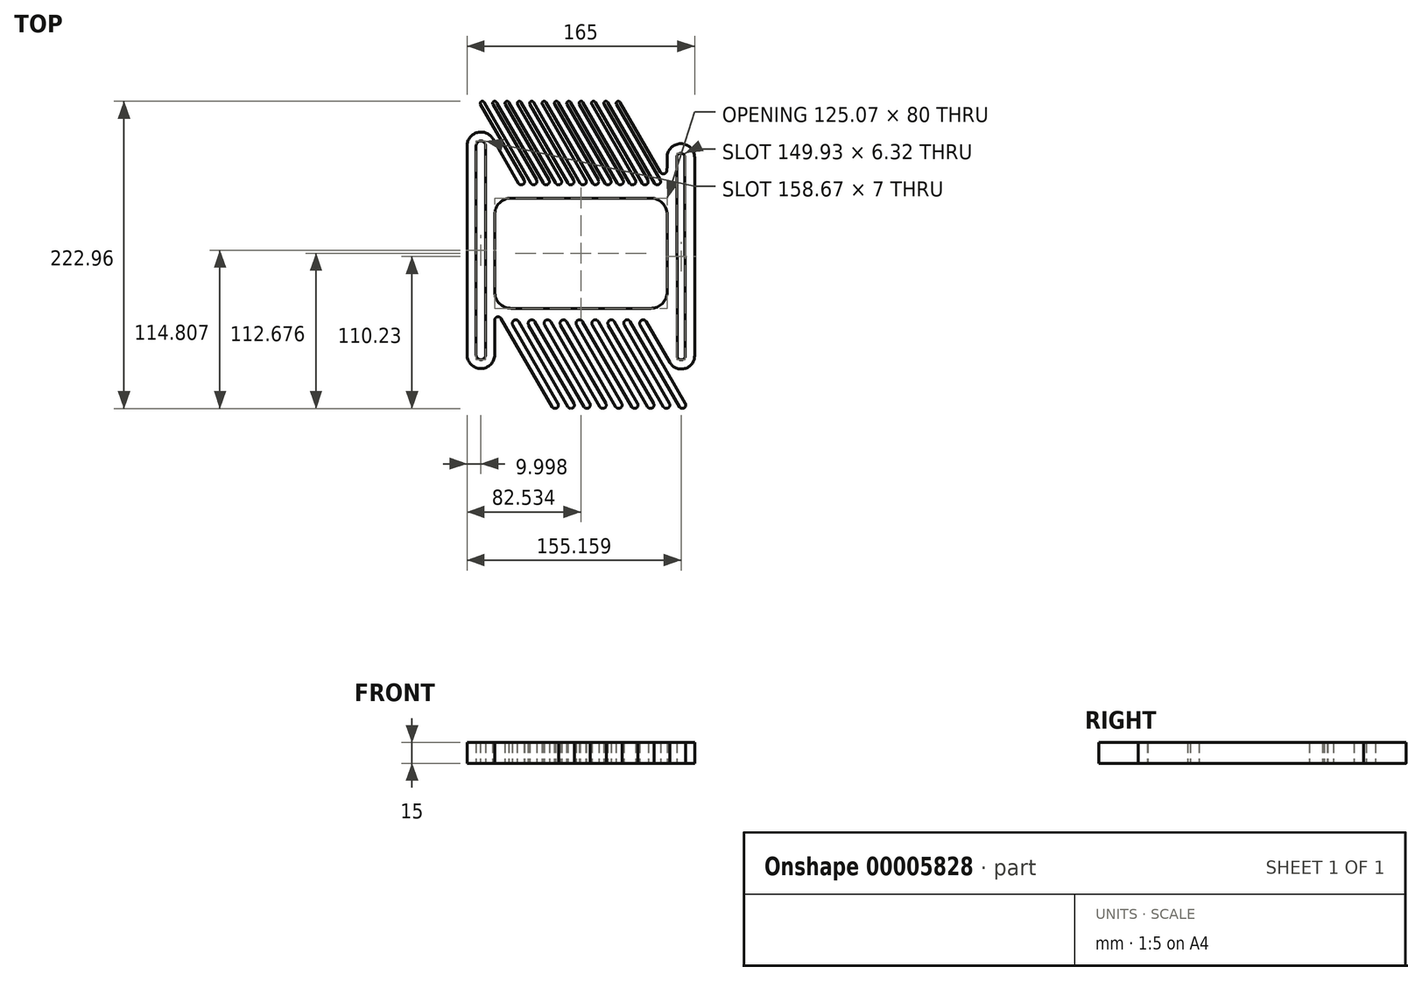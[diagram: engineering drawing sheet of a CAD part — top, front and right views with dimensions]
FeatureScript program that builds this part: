
annotation { "Feature Type Name" : "Feature", "Feature Type Description" : "" }
export const myFeature = defineFeature(function(context is Context, id is Id, definition is map)
    precondition{}
    {
        {
            var Q0;
            Q0=qCreatedBy(makeId("Top.planeOp"),FACE);
            var sketch = newSketch(context, id + "F0", { "sketchPlane" : qUnion([Q0])});
            skLineSegment(sketch, "E0.left", {"start": v(-82.57, 75.85) * mm, "end": v(-82.57, -75.82) * mm});
            skLineSegment(sketch, "E0.right", {"start": v(-62.57, 25.89) * mm, "end": v(-62.57, -30.11) * mm});
            skArc(sketch, "E1", {"start": v(-63.91, 80.85) * mm, "mid": v(-75.16, 85.51) * mm, "end": v(-82.57, 75.85) * mm});
            skArc(sketch, "E2", {"start": v(-82.57, -75.82) * mm, "mid": v(-72.57, -85.82) * mm, "end": v(-62.57, -75.82) * mm});
            skLineSegment(sketch, "E3.left", {"start": v(62.43, 67.4) * mm, "end": v(62.43, 59.57) * mm});
            skLineSegment(sketch, "E3.right", {"start": v(82.43, 67.4) * mm, "end": v(82.43, -76.53) * mm});
            skArc(sketch, "E4", {"start": v(82.43, 67.4) * mm, "mid": v(72.43, 77.4) * mm, "end": v(62.43, 67.4) * mm});
            skArc(sketch, "E5", {"start": v(64.37, -81.36) * mm, "mid": v(75.26, -85.87) * mm, "end": v(82.43, -76.53) * mm});
            skLineSegment(sketch, "E6.top", {"start": v(50.5, 37.89) * mm, "end": v(-50.57, 37.89) * mm});
            skLineSegment(sketch, "E7.bottom", {"start": v(-50.57, -42.11) * mm, "end": v(50.5, -42.11) * mm});
            skLineSegment(sketch, "E8", {"start": v(72.43, 67.4) * mm, "end": v(72.75, -76.53) * mm, "construction": true});
            skLineSegment(sketch, "E9", {"start": v(-72.57, -75.82) * mm, "end": v(-72.57, 75.85) * mm, "construction": true});
            skArc(sketch, "E10.0.startCap", {"start": v(-69.07, -75.82) * mm, "mid": v(-72.57, -79.32) * mm, "end": v(-76.07, -75.82) * mm});
            skArc(sketch, "E10.0.endCap", {"start": v(-76.07, 75.85) * mm, "mid": v(-72.57, 79.35) * mm, "end": v(-69.07, 75.85) * mm});
            skLineSegment(sketch, "E10.0.left", {"start": v(-76.07, -75.82) * mm, "end": v(-76.07, 75.85) * mm});
            skLineSegment(sketch, "E10.0.right", {"start": v(-69.07, -75.82) * mm, "end": v(-69.07, 75.85) * mm});
            skArc(sketch, "E11.0.startCap", {"start": v(69.43, 67.4) * mm, "mid": v(72.42, 70.4) * mm, "end": v(75.43, 67.41) * mm});
            skArc(sketch, "E11.0.endCap", {"start": v(75.75, -76.52) * mm, "mid": v(72.76, -79.53) * mm, "end": v(69.75, -76.53) * mm});
            skLineSegment(sketch, "E11.0.left", {"start": v(75.43, 67.41) * mm, "end": v(75.75, -76.52) * mm});
            skLineSegment(sketch, "E11.0.right", {"start": v(69.43, 67.4) * mm, "end": v(69.75, -76.53) * mm});
            skLineSegment(sketch, "E12", {"start": v(62.75, -76.53) * mm, "end": v(82.43, -76.53) * mm, "construction": true});
            skLineSegment(sketch, "E13", {"start": v(-63.91, 80.85) * mm, "end": v(-45.34, 48.68) * mm});
            skLineSegment(sketch, "E14", {"start": v(-72.84, 105.92) * mm, "end": v(-41.2, 51.14) * mm});
            skLineSegment(sketch, "E15.0", {"start": v(-70.24, 107.42) * mm, "end": v(-36.36, 48.75) * mm});
            skArc(sketch, "E16", {"start": v(-70.24, 107.42) * mm, "mid": v(-72.29, 107.97) * mm, "end": v(-72.84, 105.92) * mm});
            skLineSegment(sketch, "E17.1.0.0", {"start": v(-63.87, 105.92) * mm, "end": v(-32.17, 51.02) * mm});
            skLineSegment(sketch, "E17.1.0.1", {"start": v(-61.28, 107.42) * mm, "end": v(-60.84, 106.67) * mm});
            skArc(sketch, "E17.1.0.2", {"start": v(-61.28, 107.42) * mm, "mid": v(-63.33, 107.97) * mm, "end": v(-63.87, 105.92) * mm});
            skLineSegment(sketch, "E17.2.0.0", {"start": v(-54.87, 105.92) * mm, "end": v(-23.2, 51.07) * mm});
            skArc(sketch, "E17.2.0.2", {"start": v(-52.28, 107.44) * mm, "mid": v(-54.33, 107.97) * mm, "end": v(-54.87, 105.92) * mm});
            skLineSegment(sketch, "E17.3.0.0", {"start": v(-45.95, 105.92) * mm, "end": v(-14.2, 50.94) * mm});
            skLineSegment(sketch, "E17.3.0.1", {"start": v(-43.35, 107.42) * mm, "end": v(-9.46, 48.73) * mm});
            skArc(sketch, "E17.3.0.2", {"start": v(-43.35, 107.42) * mm, "mid": v(-45.4, 107.97) * mm, "end": v(-45.95, 105.92) * mm});
            skLineSegment(sketch, "E17.4.0.0", {"start": v(-36.98, 105.92) * mm, "end": v(-5.33, 51.12) * mm});
            skLineSegment(sketch, "E17.4.0.1", {"start": v(-34.38, 107.42) * mm, "end": v(-0.5, 48.73) * mm});
            skArc(sketch, "E17.4.0.2", {"start": v(-34.38, 107.42) * mm, "mid": v(-36.43, 107.97) * mm, "end": v(-36.98, 105.92) * mm});
            skLineSegment(sketch, "E17.5.0.0", {"start": v(-28.02, 105.92) * mm, "end": v(3.63, 51.1) * mm});
            skLineSegment(sketch, "E17.5.0.1", {"start": v(-25.42, 107.42) * mm, "end": v(8.48, 48.72) * mm});
            skArc(sketch, "E17.5.0.2", {"start": v(-25.42, 107.42) * mm, "mid": v(-27.47, 107.97) * mm, "end": v(-28.02, 105.92) * mm});
            skLineSegment(sketch, "E17.6.0.0", {"start": v(-19.05, 105.92) * mm, "end": v(12.6, 51.1) * mm});
            skLineSegment(sketch, "E17.6.0.1", {"start": v(-16.46, 107.42) * mm, "end": v(17.44, 48.72) * mm});
            skArc(sketch, "E17.6.0.2", {"start": v(-16.46, 107.42) * mm, "mid": v(-18.5, 107.97) * mm, "end": v(-19.05, 105.92) * mm});
            skLineSegment(sketch, "E17.7.0.0", {"start": v(-10.09, 105.92) * mm, "end": v(21.57, 51.1) * mm});
            skLineSegment(sketch, "E17.7.0.1", {"start": v(-7.5, 107.42) * mm, "end": v(26.41, 48.71) * mm});
            skArc(sketch, "E17.7.0.2", {"start": v(-7.5, 107.42) * mm, "mid": v(-9.54, 107.97) * mm, "end": v(-10.09, 105.92) * mm});
            skLineSegment(sketch, "E17.8.0.0", {"start": v(-1.13, 105.92) * mm, "end": v(30.53, 51.1) * mm});
            skLineSegment(sketch, "E17.8.0.1", {"start": v(1.47, 107.42) * mm, "end": v(35.38, 48.7) * mm});
            skArc(sketch, "E17.8.0.2", {"start": v(1.47, 107.42) * mm, "mid": v(-0.58, 107.97) * mm, "end": v(-1.13, 105.92) * mm});
            skLineSegment(sketch, "E17.9.0.0", {"start": v(7.83, 105.92) * mm, "end": v(39.5, 51.08) * mm});
            skLineSegment(sketch, "E17.9.0.1", {"start": v(10.43, 107.42) * mm, "end": v(44.34, 48.7) * mm});
            skArc(sketch, "E17.9.0.2", {"start": v(10.43, 107.42) * mm, "mid": v(8.38, 107.97) * mm, "end": v(7.83, 105.92) * mm});
            skLineSegment(sketch, "E17.10.0.0", {"start": v(16.8, 105.92) * mm, "end": v(48.46, 51.08) * mm});
            skLineSegment(sketch, "E17.10.0.1", {"start": v(19.4, 107.42) * mm, "end": v(53.3, 48.7) * mm});
            skArc(sketch, "E17.10.0.2", {"start": v(19.4, 107.42) * mm, "mid": v(17.35, 107.97) * mm, "end": v(16.8, 105.92) * mm});
            skLineSegment(sketch, "E17.11.0.0", {"start": v(25.76, 105.92) * mm, "end": v(57.43, 51.07) * mm});
            skLineSegment(sketch, "E17.11.0.1", {"start": v(28.36, 107.42) * mm, "end": v(57.63, 56.73) * mm});
            skArc(sketch, "E17.11.0.2", {"start": v(28.36, 107.42) * mm, "mid": v(26.3, 107.97) * mm, "end": v(25.76, 105.92) * mm});
            skLineSegment(sketch, "E18.filletArc", {"start": v(47.06, 60.31) * mm, "end": v(47.06, 60.31) * mm});
            skArc(sketch, "E19.filletArc", {"start": v(-62.57, -30.11) * mm, "mid": v(-59.06, -38.6) * mm, "end": v(-50.57, -42.11) * mm});
            skPoint(sketch, "E20.visualSharp", {"position": v(-58.86, -51.71) * mm});
            skLineSegment(sketch, "E21", {"start": v(62.5, -30.11) * mm, "end": v(62.5, 25.89) * mm});
            skPoint(sketch, "E22.visualSharp", {"position": v(62.5, -42.11) * mm});
            skArc(sketch, "E22.filletArc", {"start": v(50.5, -42.11) * mm, "mid": v(58.99, -38.6) * mm, "end": v(62.5, -30.11) * mm});
            skArc(sketch, "E23.filletArc", {"start": v(62.5, 25.89) * mm, "mid": v(58.99, 34.37) * mm, "end": v(50.5, 37.89) * mm});
            skArc(sketch, "E24.filletArc", {"start": v(-50.57, 37.89) * mm, "mid": v(-59.06, 34.37) * mm, "end": v(-62.57, 25.89) * mm});
            skArc(sketch, "E25.trimOffspring", {"start": v(62.26, 57.56) * mm, "mid": v(62.39, 58.56) * mm, "end": v(62.43, 59.57) * mm});
            skLineSegment(sketch, "E26", {"start": v(-72.84, 105.92) * mm, "end": v(-70.24, 107.42) * mm, "construction": true});
            skLineSegment(sketch, "E27", {"start": v(-71.54, 106.67) * mm, "end": v(47, 106.67) * mm, "construction": true});
            skArc(sketch, "E28", {"start": v(-45.34, 48.68) * mm, "mid": v(-42.03, 47.82) * mm, "end": v(-41.2, 51.14) * mm});
            skArc(sketch, "E29.2.0.0", {"start": v(-27.33, 48.78) * mm, "mid": v(-24.1, 47.82) * mm, "end": v(-23.2, 51.07) * mm});
            skArc(sketch, "E30.0.3.0", {"start": v(-18.43, 48.82) * mm, "mid": v(-15.26, 47.77) * mm, "end": v(-14.2, 50.94) * mm});
            skArc(sketch, "E30.0.4.0", {"start": v(-9.46, 48.73) * mm, "mid": v(-6.18, 47.82) * mm, "end": v(-5.33, 51.12) * mm});
            skArc(sketch, "E30.0.5.0", {"start": v(-0.5, 48.73) * mm, "mid": v(2.78, 47.82) * mm, "end": v(3.63, 51.1) * mm});
            skArc(sketch, "E30.0.6.0", {"start": v(8.48, 48.72) * mm, "mid": v(11.73, 47.85) * mm, "end": v(12.6, 51.1) * mm});
            skArc(sketch, "E30.0.7.0", {"start": v(17.44, 48.72) * mm, "mid": v(20.7, 47.85) * mm, "end": v(21.57, 51.1) * mm});
            skArc(sketch, "E30.0.8.0", {"start": v(26.41, 48.71) * mm, "mid": v(29.66, 47.84) * mm, "end": v(30.53, 51.1) * mm});
            skArc(sketch, "E30.0.9.0", {"start": v(35.38, 48.7) * mm, "mid": v(38.63, 47.83) * mm, "end": v(39.5, 51.08) * mm});
            skArc(sketch, "E30.0.10.0", {"start": v(44.34, 48.7) * mm, "mid": v(47.6, 47.82) * mm, "end": v(48.46, 51.08) * mm});
            skArc(sketch, "E30.0.11.0", {"start": v(53.3, 48.7) * mm, "mid": v(56.56, 47.82) * mm, "end": v(57.43, 51.07) * mm});
            skPoint(sketch, "E31.trimOffspring.end.orphan", {"position": v(-39.14, 47.57) * mm});
            skLineSegment(sketch, "E32.trimOffspring", {"start": v(-39.8, 61.5) * mm, "end": v(-39.8, 61.5) * mm});
            skPoint(sketch, "E33.orphan", {"position": v(-44.68, 47.54) * mm});
            skLineSegment(sketch, "E34", {"start": v(-27.33, 48.78) * mm, "end": v(-60.84, 106.67) * mm});
            skLineSegment(sketch, "E35", {"start": v(-18.43, 48.82) * mm, "end": v(-52.28, 107.44) * mm});
            skArc(sketch, "E36.filletArc", {"start": v(57.63, 56.73) * mm, "mid": v(60.24, 55.52) * mm, "end": v(62.26, 57.56) * mm});
            skLineSegment(sketch, "E37", {"start": v(-43.26, 49.89) * mm, "end": v(55.37, 49.89) * mm, "construction": true});
            skArc(sketch, "E38", {"start": v(-36.36, 48.75) * mm, "mid": v(-33.16, 47.85) * mm, "end": v(-32.17, 51.02) * mm});
            skPoint(sketch, "E39", {"position": v(0, 0) * mm});
            skLineSegment(sketch, "E40.left", {"start": v(-62.57, -75.82) * mm, "end": v(-62.57, -50.76) * mm});
            skLineSegment(sketch, "E41.11.0.1", {"start": v(-20.98, -113.54) * mm, "end": v(-57.94, -49.52) * mm});
            skArc(sketch, "E42.filletArc", {"start": v(-57.94, -49.52) * mm, "mid": v(-60.73, -48.36) * mm, "end": v(-62.57, -50.76) * mm});
            skLineSegment(sketch, "E43", {"start": v(-20.98, -113.54) * mm, "end": v(-16.65, -111.04) * mm, "construction": true});
            skArc(sketch, "E44.11.0.2", {"start": v(-20.98, -113.54) * mm, "mid": v(-17.56, -114.45) * mm, "end": v(-16.65, -111.04) * mm});
            skLineSegment(sketch, "E45", {"start": v(37.01, -52.96) * mm, "end": v(-243.4, -52.96) * mm, "construction": true});
            skArc(sketch, "E46", {"start": v(-45.13, -51.71) * mm, "mid": v(-48.54, -50.8) * mm, "end": v(-49.46, -54.21) * mm});
            skLineSegment(sketch, "E47", {"start": v(-16.65, -111.04) * mm, "end": v(-49.46, -54.21) * mm});
            skLineSegment(sketch, "E48", {"start": v(-45.13, -51.71) * mm, "end": v(-9.43, -113.54) * mm});
            skLineSegment(sketch, "E49", {"start": v(-18.81, -112.29) * mm, "end": v(74.16, -111.04) * mm, "construction": true});
            skLineSegment(sketch, "E50", {"start": v(-20.98, -113.54) * mm, "end": v(73.8, -113.54) * mm, "construction": true});
            skArc(sketch, "E51.1.0.0", {"start": v(-9.43, -113.54) * mm, "mid": v(-6.02, -114.45) * mm, "end": v(-5.1, -111.04) * mm});
            skLineSegment(sketch, "E51.1.0.1", {"start": v(-5.1, -111.04) * mm, "end": v(-37.9, -54.21) * mm});
            skArc(sketch, "E51.1.0.2", {"start": v(-33.58, -51.71) * mm, "mid": v(-37, -50.8) * mm, "end": v(-37.9, -54.21) * mm});
            skLineSegment(sketch, "E51.1.0.3", {"start": v(-33.58, -51.71) * mm, "end": v(2.12, -113.54) * mm});
            skArc(sketch, "E51.2.0.0", {"start": v(2.12, -113.54) * mm, "mid": v(5.53, -114.45) * mm, "end": v(6.45, -111.04) * mm});
            skLineSegment(sketch, "E51.2.0.1", {"start": v(6.45, -111.04) * mm, "end": v(-26.36, -54.21) * mm});
            skArc(sketch, "E51.2.0.2", {"start": v(-22.03, -51.71) * mm, "mid": v(-25.45, -50.8) * mm, "end": v(-26.36, -54.21) * mm});
            skLineSegment(sketch, "E51.2.0.3", {"start": v(-22.03, -51.71) * mm, "end": v(13.66, -113.54) * mm});
            skArc(sketch, "E51.3.0.0", {"start": v(13.66, -113.54) * mm, "mid": v(17.08, -114.45) * mm, "end": v(18, -111.04) * mm});
            skLineSegment(sketch, "E51.3.0.1", {"start": v(18, -111.04) * mm, "end": v(-14.82, -54.21) * mm});
            skArc(sketch, "E51.3.0.2", {"start": v(-10.49, -51.71) * mm, "mid": v(-13.9, -50.8) * mm, "end": v(-14.82, -54.21) * mm});
            skLineSegment(sketch, "E51.3.0.3", {"start": v(-10.49, -51.71) * mm, "end": v(25.21, -113.54) * mm});
            skArc(sketch, "E51.4.0.0", {"start": v(25.21, -113.54) * mm, "mid": v(28.63, -114.45) * mm, "end": v(29.54, -111.04) * mm});
            skLineSegment(sketch, "E51.4.0.1", {"start": v(29.54, -111.04) * mm, "end": v(-3.27, -54.21) * mm});
            skArc(sketch, "E51.4.0.2", {"start": v(1.06, -51.71) * mm, "mid": v(-2.35, -50.8) * mm, "end": v(-3.27, -54.21) * mm});
            skLineSegment(sketch, "E51.4.0.3", {"start": v(1.06, -51.71) * mm, "end": v(36.76, -113.54) * mm});
            skArc(sketch, "E51.5.0.0", {"start": v(36.76, -113.54) * mm, "mid": v(40.17, -114.45) * mm, "end": v(41.09, -111.04) * mm});
            skLineSegment(sketch, "E51.5.0.1", {"start": v(41.09, -111.04) * mm, "end": v(8.28, -54.21) * mm});
            skArc(sketch, "E51.5.0.2", {"start": v(12.6, -51.71) * mm, "mid": v(9.2, -50.8) * mm, "end": v(8.28, -54.21) * mm});
            skLineSegment(sketch, "E51.5.0.3", {"start": v(12.6, -51.71) * mm, "end": v(48.3, -113.54) * mm});
            skArc(sketch, "E51.6.0.0", {"start": v(48.3, -113.54) * mm, "mid": v(51.72, -114.45) * mm, "end": v(52.63, -111.04) * mm});
            skLineSegment(sketch, "E51.6.0.1", {"start": v(52.63, -111.04) * mm, "end": v(19.83, -54.21) * mm});
            skArc(sketch, "E51.6.0.2", {"start": v(24.16, -51.71) * mm, "mid": v(20.74, -50.8) * mm, "end": v(19.83, -54.21) * mm});
            skLineSegment(sketch, "E51.6.0.3", {"start": v(24.16, -51.71) * mm, "end": v(59.85, -113.54) * mm});
            skArc(sketch, "E51.7.0.0", {"start": v(59.85, -113.54) * mm, "mid": v(63.27, -114.45) * mm, "end": v(64.18, -111.04) * mm});
            skLineSegment(sketch, "E51.7.0.1", {"start": v(64.18, -111.04) * mm, "end": v(31.37, -54.21) * mm});
            skArc(sketch, "E51.7.0.2", {"start": v(35.7, -51.71) * mm, "mid": v(32.29, -50.8) * mm, "end": v(31.37, -54.21) * mm});
            skLineSegment(sketch, "E51.7.0.3", {"start": v(35.7, -51.71) * mm, "end": v(71.4, -113.54) * mm});
            skArc(sketch, "E51.8.0.0", {"start": v(71.4, -113.54) * mm, "mid": v(74.81, -114.45) * mm, "end": v(75.73, -111.04) * mm});
            skLineSegment(sketch, "E51.8.0.1", {"start": v(75.73, -111.04) * mm, "end": v(42.92, -54.21) * mm});
            skArc(sketch, "E51.8.0.2", {"start": v(47.25, -51.71) * mm, "mid": v(43.83, -50.8) * mm, "end": v(42.92, -54.21) * mm});
            skLineSegment(sketch, "E51.direction1", {"start": v(-20.98, -113.54) * mm, "end": v(-9.43, -113.54) * mm, "construction": true});
            skLineSegment(sketch, "E52", {"start": v(64.37, -81.36) * mm, "end": v(47.25, -51.71) * mm});
            skSolve(sketch);
        }
        {
            var Q0;
            Q0=makeQuery(id+"F0.imprint","IMPRINT",FACE,{"disambiguationData":[TD([[makeQuery(id+"F0.imprint","IMPRINT",EDGE,{"derivedFrom":sQuery(id+"F0.wireOp",EDGE,"E0.left")}),1.0]])]});
            extrude(context, id + "F1", {"entities" : qUnion([Q0]), "depth" : 15 * mm, "offsetDistance" : 25 * mm});
        }
    });
